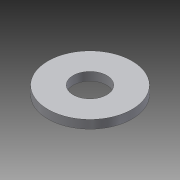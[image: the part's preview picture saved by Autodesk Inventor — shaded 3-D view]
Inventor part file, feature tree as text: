
AUTODESK INVENTOR PART (.ipt)
format: ipt  version: 2015 (Build 190159000, 159)  size: 76,800 bytes
history: native  units: in
note: dims shown in document units (in); Inventor stores cm internally (conversion verified against a paired STEP export)
features: extrude x1, sketch x1
ambient origin geometry x8: Origin, YZ Plane, XZ Plane, XY Plane, X Axis, Y Axis, Z Axis, Center Point
bodies: Solid1 (feature_tree)
feature tree (2):
  extrude  "Extrusion1"  Depth=0.0625in
  sketch  "Sketch1"  dims[d0=0.25in d1=0.625in d2=0.0625in d3=0.0in]
